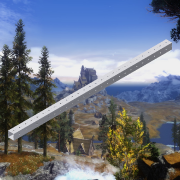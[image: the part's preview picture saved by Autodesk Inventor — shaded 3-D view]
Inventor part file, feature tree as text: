
AUTODESK INVENTOR PART (.ipt)
format: ipt  version: 2015 SP1 (Build 190203100, 203)  size: 1,390,080 bytes
history: native  units: in
note: dims shown in document units (in); Inventor stores cm internally (conversion verified against a paired STEP export)
features: other x2, extrude x2, sketch x2, plane x1, imported_body x1
ambient origin geometry x8: Origin, YZ Plane, XZ Plane, XY Plane, X Axis, Y Axis, Z Axis, Center Point
bodies: Body1 (feature_tree)
feature tree (8):
  other  "LPattern2"
  other  "VersaFrame 1 x 1 x 0.040 Pre-Drilled Tube Stock (59 length)(217-3426)1"
  plane  "Work Plane1"
  extrude  "Extrusion1"  Depth=1.0in TaperAngle=0.0deg
  extrude  "Extrusion2"  Depth=1.0in TaperAngle=0.0deg
  imported_body  "Base1"
  sketch  "Sketch1"  dims[d0=28.0in d1=1.0in d2=0.0in]
  sketch  "Sketch2"  dims[d3=1.0in d4=1.0in d5=0.0in]
